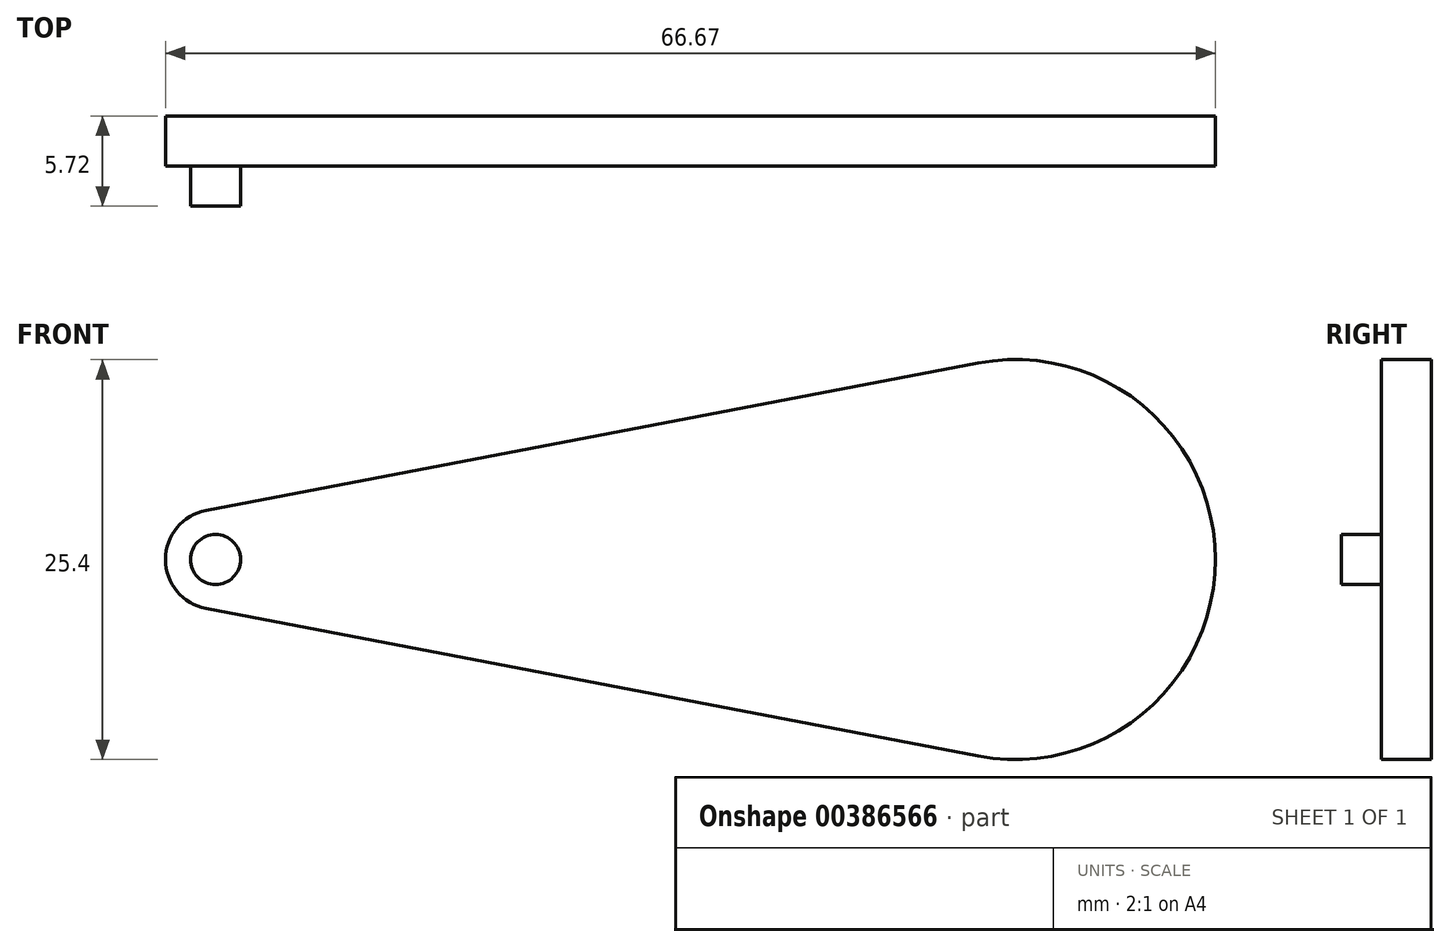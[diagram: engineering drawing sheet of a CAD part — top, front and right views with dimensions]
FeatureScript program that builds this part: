
annotation { "Feature Type Name" : "Feature", "Feature Type Description" : "" }
export const myFeature = defineFeature(function(context is Context, id is Id, definition is map)
    precondition{}
    {
        {
            var Q0;
            Q0=qCreatedBy(makeId("Front.planeOp"),FACE);
            var sketch = newSketch(context, id + "F0", { "sketchPlane" : qUnion([Q0])});
            skArc(sketch, "E0", {"start": v(-2.38, -12.47) * mm, "mid": v(12.7, 0) * mm, "end": v(-2.38, 12.47) * mm});
            skArc(sketch, "E1", {"start": v(-51.4, 3.12) * mm, "mid": v(-53.98, 0) * mm, "end": v(-51.4, -3.12) * mm});
            skLineSegment(sketch, "E2", {"start": v(-51.4, 3.12) * mm, "end": v(-2.38, 12.47) * mm});
            skLineSegment(sketch, "E3", {"start": v(-51.4, -3.12) * mm, "end": v(-2.38, -12.47) * mm});
            skSolve(sketch);
        }
        {
            var Q0;
            Q0=makeQuery(id+"F0.imprint","IMPRINT",FACE,{"disambiguationData":[TD([[makeQuery(id+"F0.imprint","IMPRINT",EDGE,{"derivedFrom":sQuery(id+"F0.wireOp",EDGE,"E0")}),1.0]])]});
            extrude(context, id + "F1", {"entities" : qUnion([Q0]), "depth" : 3.17 * mm});
        }
        {
            var Q0;
            Q0=makeQuery(id+"F1.opExtrude","CAP_FACE",FACE,{"disambiguationData":[OSD([sQuery(id+"F0.wireOp",EDGE,"E0"),sQuery(id+"F0.wireOp",EDGE,"E1"),sQuery(id+"F0.wireOp",EDGE,"E2"),sQuery(id+"F0.wireOp",EDGE,"E3")])],"isStart":false});
            var sketch = newSketch(context, id + "F2", { "sketchPlane" : qUnion([Q0])});
            skPoint(sketch, "E4", {"position": v(-50.8, 0) * mm});
            skCircle(sketch, "E5", {"center": v(-50.8, 0) * mm, "radius": 1.59 * mm});
            skSolve(sketch);
        }
        {
            var Q0;
            Q0 = qSketchRegion(id + "F2", true);
            extrude(context, id + "F3", {"entities" : qUnion([Q0]), "operationType" : NewBodyOperationType.ADD, "depth" : 2.54 * mm});
        }
    });
